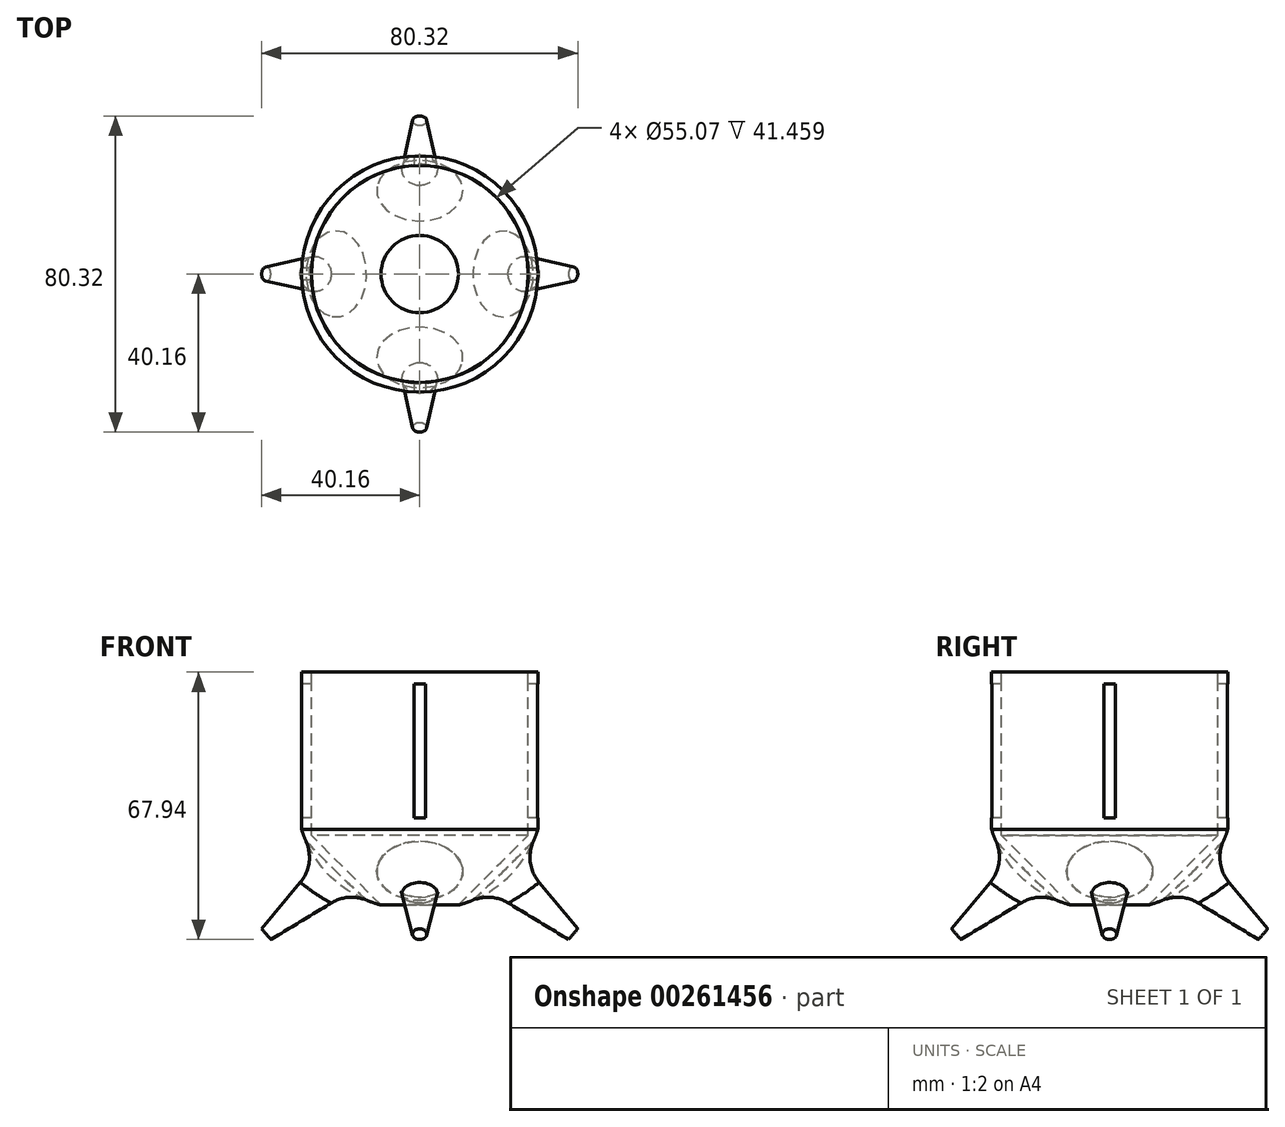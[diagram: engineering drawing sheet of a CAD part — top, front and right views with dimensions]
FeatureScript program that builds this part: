
annotation { "Feature Type Name" : "Feature", "Feature Type Description" : "" }
export const myFeature = defineFeature(function(context is Context, id is Id, definition is map)
    precondition{}
    {
        {
            var Q0;
            Q0=qCreatedBy(makeId("Front.planeOp"),FACE);
            var sketch = newSketch(context, id + "F0", { "sketchPlane" : qUnion([Q0])});
            skLineSegment(sketch, "E0", {"start": v(0, 25.7) * mm, "end": v(0, -34.3) * mm});
            skLineSegment(sketch, "E1", {"start": v(0, 25.7) * mm, "end": v(-30, 25.7) * mm});
            skLineSegment(sketch, "E2", {"start": v(-30, 25.7) * mm, "end": v(-30, -14.3) * mm});
            skArc(sketch, "E3", {"start": v(-30, -14.3) * mm, "mid": v(-18.51, -29.56) * mm, "end": v(0, -34.3) * mm});
            skSolve(sketch);
        }
        {
            var Q0;
            Q0=makeQuery(id+"F0.imprint","IMPRINT",FACE,{"disambiguationData":[TD([[makeQuery(id+"F0.imprint","IMPRINT",EDGE,{"derivedFrom":sQuery(id+"F0.wireOp",EDGE,"E0")}),-1.0]])]});
            var Q1;
            Q1=sQuery(id+"F0.wireOp",EDGE,"E0");
            revolve(context, id + "F1", {"entities" : qUnion([Q0]), "axis" : qUnion([Q1]), "revolveType" : RevolveType.FULL});
        }
        {
            var Q0;
            Q0=qCreatedBy(makeId("Front.planeOp"),FACE);
            var sketch = newSketch(context, id + "F2", { "sketchPlane" : qUnion([Q0])});
            skLineSegment(sketch, "E4", {"start": v(-17.6, -22.48) * mm, "end": v(-38.98, -40.87) * mm});
            skLineSegment(sketch, "E5", {"start": v(-38.98, -40.87) * mm, "end": v(-37.8, -42.24) * mm});
            skLineSegment(sketch, "E6", {"start": v(-37.8, -42.24) * mm, "end": v(-14.3, -27.98) * mm});
            skLineSegment(sketch, "E7", {"start": v(-14.3, -27.98) * mm, "end": v(-19.44, -24.06) * mm});
            skSolve(sketch);
        }
        {
            var Q0;
            Q0=qSketchRegion(id+"F2",true);
            var Q1;
            Q1=sQuery(id+"F2.wireOp",EDGE,"E4");
            revolve(context, id + "F3", {"operationType" : NewBodyOperationType.ADD, "entities" : qUnion([Q0]), "axis" : qUnion([Q1]), "revolveType" : RevolveType.FULL});
        }
        {
            var Q0;
            Q0=makeQuery(id+"F1.opRevolve","SWEPT_BODY",BODY,{"disambiguationData":[OSD([sQuery(id+"F0.wireOp",EDGE,"E0"),sQuery(id+"F0.wireOp",EDGE,"E1"),sQuery(id+"F0.wireOp",EDGE,"E2"),sQuery(id+"F0.wireOp",EDGE,"E3")])]});
            var Q1;
            Q1=makeQuery(id+"F1.opRevolve","SWEPT_EDGE",EDGE,{"disambiguationData":[OSD([sQuery(id+"F0.wireOp",EDGE,"E1"),sQuery(id+"F0.wireOp",EDGE,"E2")])]});
            circularPattern(context, id + "F4", {"entities" : qUnion([Q0]), "axis" : qUnion([Q1]), "angle" : 360 * degree, "instanceCount" : 4, "equalSpace" : true});
        }
        {
            var Q0;
            Q0=qCreatedBy(makeId("Front.planeOp"),FACE);
            var sketch = newSketch(context, id + "F5", { "sketchPlane" : qUnion([Q0])});
            skLineSegment(sketch, "E8", {"start": v(0, 25.7) * mm, "end": v(-27.53, 25.7) * mm});
            skLineSegment(sketch, "E9", {"start": v(-27.53, 25.7) * mm, "end": v(-27.53, -15.75) * mm});
            skLineSegment(sketch, "E10", {"start": v(-27.53, -15.75) * mm, "end": v(-4.62, -38.67) * mm});
            skLineSegment(sketch, "E11", {"start": v(-4.62, -38.67) * mm, "end": v(0, -38.67) * mm});
            skLineSegment(sketch, "E12", {"start": v(0, -38.67) * mm, "end": v(0, 25.7) * mm});
            skSolve(sketch);
        }
        {
            var Q0;
            Q0=qSketchRegion(id+"F5",true);
            var Q1;
            Q1=sQuery(id+"F5.wireOp",EDGE,"E12");
            revolve(context, id + "F6", {"operationType" : NewBodyOperationType.REMOVE, "entities" : qUnion([Q0]), "axis" : qUnion([Q1]), "revolveType" : RevolveType.FULL, "oppositeDirection" : true});
        }
        {
            var Q0;
            Q0=qCreatedBy(makeId("Front.planeOp"),FACE);
            var sketch = newSketch(context, id + "F7", { "sketchPlane" : qUnion([Q0])});
            skLineSegment(sketch, "E13", {"start": v(0, 25.7) * mm, "end": v(0, -14.3) * mm});
            skLineSegment(sketch, "E14.bottom", {"start": v(1.5, -11.3) * mm, "end": v(-1.5, -11.3) * mm});
            skLineSegment(sketch, "E14.top", {"start": v(1.5, 22.7) * mm, "end": v(-1.5, 22.7) * mm});
            skLineSegment(sketch, "E14.left", {"start": v(1.5, -11.3) * mm, "end": v(1.5, 22.7) * mm});
            skLineSegment(sketch, "E14.right", {"start": v(-1.5, -11.3) * mm, "end": v(-1.5, 22.7) * mm});
            skPoint(sketch, "E14.middle", {"position": v(0, 5.7) * mm});
            skSolve(sketch);
        }
        {
            var Q0;
            Q0=qSketchRegion(id+"F7",true);
            extrude(context, id + "F8", {"entities" : qUnion([Q0]), "operationType" : NewBodyOperationType.REMOVE, "endBound" : BoundingType.THROUGH_ALL, "oppositeDirection" : true, "depth" : 25 * mm, "hasSecondDirection" : true, "secondDirectionBound" : SecondDirectionBoundingType.THROUGH_ALL, "secondDirectionOppositeDirection" : false, "secondDirectionDepth" : 25 * mm});
        }
        {
            var Q0;
            Q0=qCreatedBy(makeId("Right.planeOp"),FACE);
            var sketch = newSketch(context, id + "F9", { "sketchPlane" : qUnion([Q0])});
            skLineSegment(sketch, "E15", {"start": v(0, 25.7) * mm, "end": v(0, -14.3) * mm});
            skLineSegment(sketch, "E16.bottom", {"start": v(1.5, -11.3) * mm, "end": v(-1.5, -11.3) * mm});
            skLineSegment(sketch, "E16.top", {"start": v(1.5, 22.7) * mm, "end": v(-1.5, 22.7) * mm});
            skLineSegment(sketch, "E16.left", {"start": v(1.5, -11.3) * mm, "end": v(1.5, 22.7) * mm});
            skLineSegment(sketch, "E16.right", {"start": v(-1.5, -11.3) * mm, "end": v(-1.5, 22.7) * mm});
            skPoint(sketch, "E16.middle", {"position": v(0, 5.7) * mm});
            skSolve(sketch);
        }
        {
            var Q0;
            Q0=qSketchRegion(id+"F9",true);
            extrude(context, id + "F10", {"entities" : qUnion([Q0]), "operationType" : NewBodyOperationType.REMOVE, "endBound" : BoundingType.THROUGH_ALL, "depth" : 25 * mm, "hasSecondDirection" : true, "secondDirectionBound" : SecondDirectionBoundingType.THROUGH_ALL, "secondDirectionOppositeDirection" : true, "secondDirectionDepth" : 25 * mm});
        }
        {
            var Q0;
            Q0=makeQuery(id+"F3.boolean.opBoolean","INTERSECT",EDGE,{"derivedFrom":[makeQuery(id+"F1.opRevolve","SWEPT_FACE",FACE,{"disambiguationData":[OSD([sQuery(id+"F0.wireOp",EDGE,"E3")])]}),makeQuery(id+"F3.opRevolve","SWEPT_FACE",FACE,{"disambiguationData":[OSD([sQuery(id+"F2.wireOp",EDGE,"E6")])]})]});
            var Q1;
            Q1=makeQuery(id+"F4.opPattern","COPY",EDGE,{"derivedFrom":makeQuery(id+"F3.boolean.opBoolean","INTERSECT",EDGE,{"derivedFrom":[makeQuery(id+"F1.opRevolve","SWEPT_FACE",FACE,{"disambiguationData":[OSD([sQuery(id+"F0.wireOp",EDGE,"E3")])]}),makeQuery(id+"F3.opRevolve","SWEPT_FACE",FACE,{"disambiguationData":[OSD([sQuery(id+"F2.wireOp",EDGE,"E6")])]})]}),"instanceName":"1"});
            var Q2;
            Q2=makeQuery(id+"F4.opPattern","COPY",EDGE,{"derivedFrom":makeQuery(id+"F3.boolean.opBoolean","INTERSECT",EDGE,{"derivedFrom":[makeQuery(id+"F1.opRevolve","SWEPT_FACE",FACE,{"disambiguationData":[OSD([sQuery(id+"F0.wireOp",EDGE,"E3")])]}),makeQuery(id+"F3.opRevolve","SWEPT_FACE",FACE,{"disambiguationData":[OSD([sQuery(id+"F2.wireOp",EDGE,"E6")])]})]}),"instanceName":"2"});
            var Q3;
            Q3=makeQuery(id+"F4.opPattern","COPY",EDGE,{"derivedFrom":makeQuery(id+"F3.boolean.opBoolean","INTERSECT",EDGE,{"derivedFrom":[makeQuery(id+"F1.opRevolve","SWEPT_FACE",FACE,{"disambiguationData":[OSD([sQuery(id+"F0.wireOp",EDGE,"E3")])]}),makeQuery(id+"F3.opRevolve","SWEPT_FACE",FACE,{"disambiguationData":[OSD([sQuery(id+"F2.wireOp",EDGE,"E6")])]})]}),"instanceName":"3"});
            fillet(context, id + "F11", {"entities" : qUnion([Q0, Q1, Q2, Q3]), "radius" : 10 * mm, "tangentPropagation" : true, "allowEdgeOverflow" : false});
        }
    });
